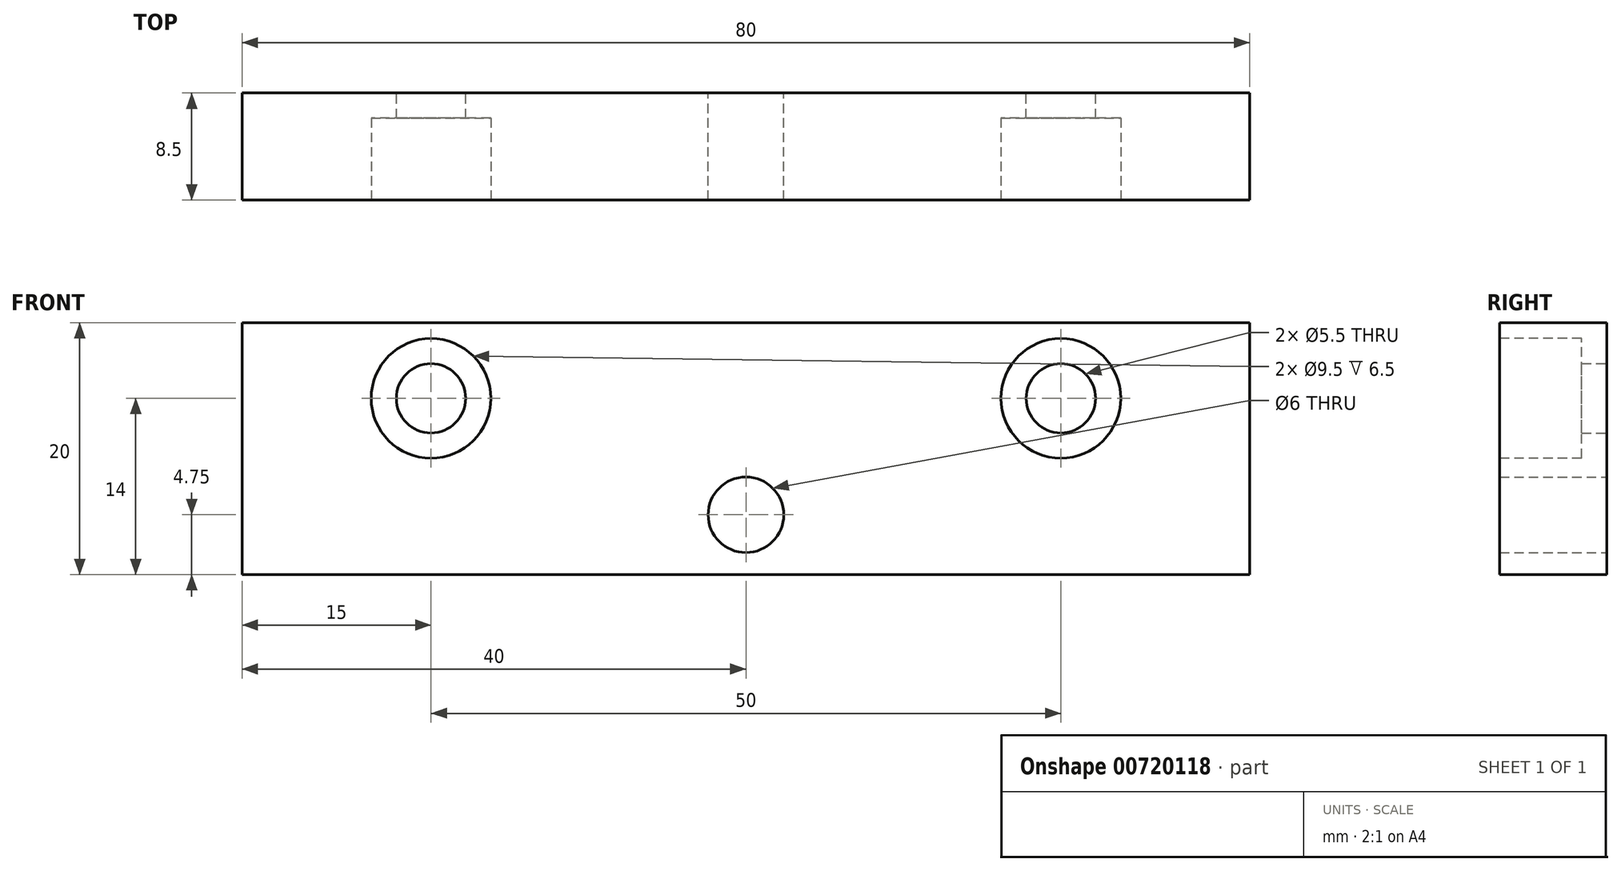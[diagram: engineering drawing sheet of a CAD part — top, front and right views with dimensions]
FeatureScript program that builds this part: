
annotation { "Feature Type Name" : "Feature", "Feature Type Description" : "" }
export const myFeature = defineFeature(function(context is Context, id is Id, definition is map)
    precondition{}
    {
        {
            var Q0;
            Q0=qCreatedBy(makeId("Front.planeOp"),FACE);
            var sketch = newSketch(context, id + "F0", { "sketchPlane" : qUnion([Q0])});
            skLineSegment(sketch, "E0.bottom", {"start": v(0, 0) * mm, "end": v(80, 0) * mm});
            skLineSegment(sketch, "E0.top", {"start": v(0, 20) * mm, "end": v(80, 20) * mm});
            skLineSegment(sketch, "E0.left", {"start": v(0, 0) * mm, "end": v(0, 20) * mm});
            skLineSegment(sketch, "E0.right", {"start": v(80, 0) * mm, "end": v(80, 20) * mm});
            skCircle(sketch, "E1", {"center": v(40, 4.75) * mm, "radius": 3 * mm});
            skPoint(sketch, "E1.centerSnap0", {"position": v(40, 0) * mm});
            skCircle(sketch, "E2", {"center": v(15, 14) * mm, "radius": 2.75 * mm});
            skCircle(sketch, "E3", {"center": v(65, 14) * mm, "radius": 2.75 * mm});
            skSolve(sketch);
        }
        {
            var Q0;
            Q0=makeQuery(id+"F0.imprint","IMPRINT",FACE,{"disambiguationData":[TD([[makeQuery(id+"F0.imprint","IMPRINT",EDGE,{"derivedFrom":sQuery(id+"F0.wireOp",EDGE,"E0.bottom")}),1.0]])]});
            extrude(context, id + "F1", {"entities" : qUnion([Q0]), "depth" : 8.5 * mm, "offsetDistance" : 25 * mm});
        }
        {
            var Q0;
            Q0=makeQuery(id+"F1.opExtrude","CAP_FACE",FACE,{"disambiguationData":[OSD([sQuery(id+"F0.wireOp",EDGE,"E0.bottom"),sQuery(id+"F0.wireOp",EDGE,"E0.top"),sQuery(id+"F0.wireOp",EDGE,"E0.left"),sQuery(id+"F0.wireOp",EDGE,"E0.right"),sQuery(id+"F0.wireOp",EDGE,"E1"),sQuery(id+"F0.wireOp",EDGE,"E2"),sQuery(id+"F0.wireOp",EDGE,"E3")])],"isStart":false});
            var sketch = newSketch(context, id + "F2", { "sketchPlane" : qUnion([Q0])});
            skCircle(sketch, "E4", {"center": v(15, 14) * mm, "radius": 4.75 * mm});
            skCircle(sketch, "E5", {"center": v(65, 14) * mm, "radius": 4.75 * mm});
            skSolve(sketch);
        }
        {
            var Q0;
            Q0=makeQuery(id+"F2.imprint","IMPRINT",FACE,{"disambiguationData":[TD([[makeQuery(id+"F2.imprint","IMPRINT",EDGE,{"derivedFrom":sQuery(id+"F2.wireOp",EDGE,"E4")}),1.0]])]});
            var Q1;
            Q1=makeQuery(id+"F2.imprint","IMPRINT",FACE,{"disambiguationData":[TD([[makeQuery(id+"F2.imprint","IMPRINT",EDGE,{"derivedFrom":sQuery(id+"F2.wireOp",EDGE,"E5")}),1.0]])]});
            extrude(context, id + "F3", {"entities" : qUnion([Q0, Q1]), "operationType" : NewBodyOperationType.REMOVE, "oppositeDirection" : true, "depth" : 6.5 * mm, "offsetDistance" : 25 * mm});
        }
    });
